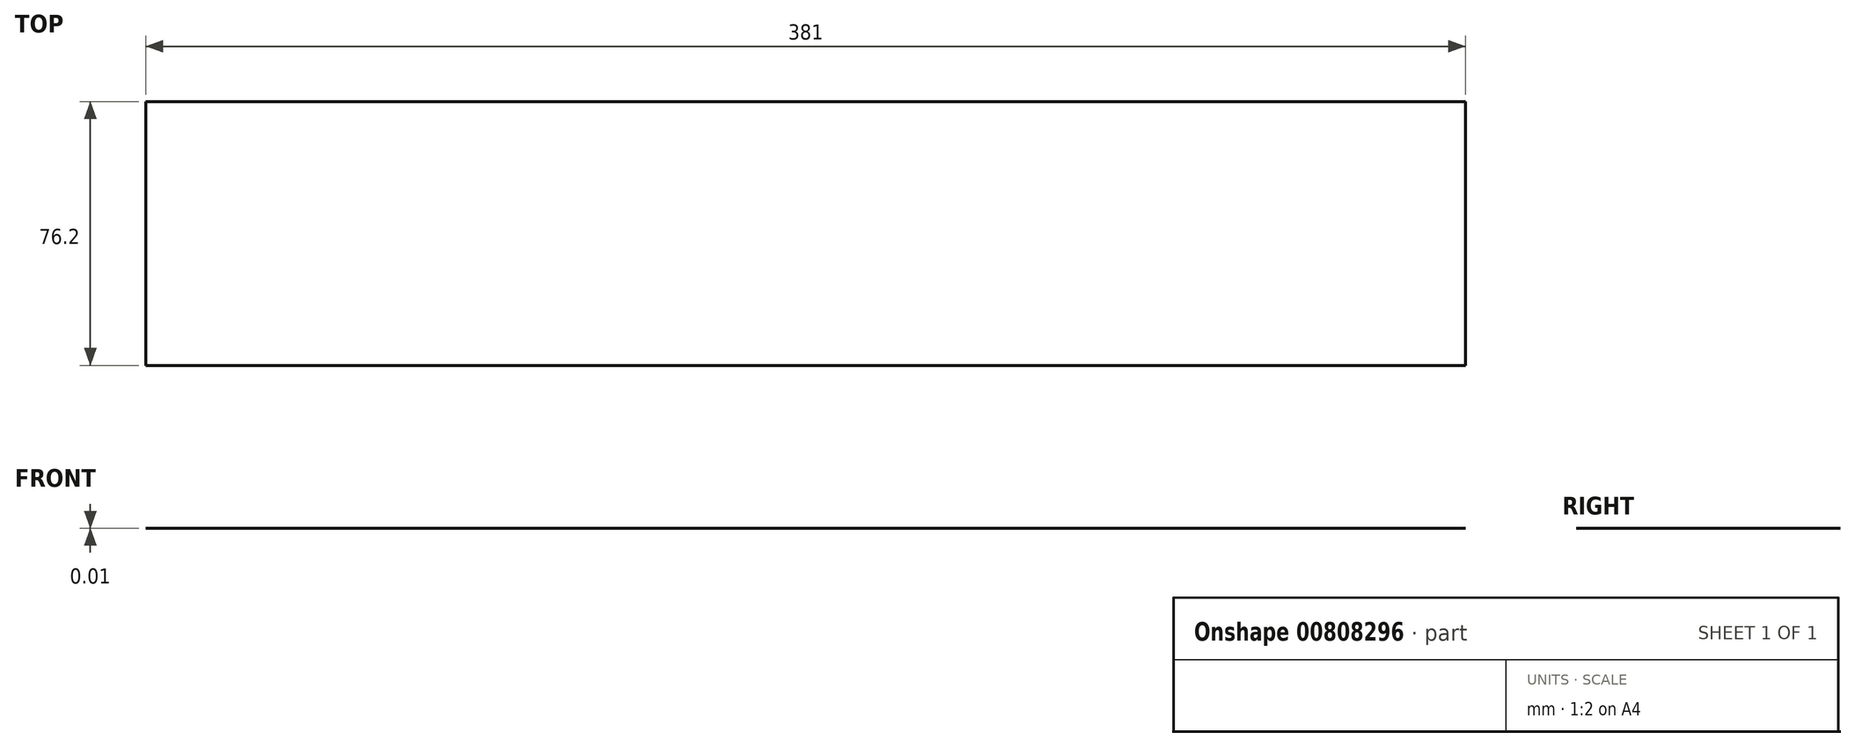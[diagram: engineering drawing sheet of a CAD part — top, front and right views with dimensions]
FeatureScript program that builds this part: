
annotation { "Feature Type Name" : "Feature", "Feature Type Description" : "" }
export const myFeature = defineFeature(function(context is Context, id is Id, definition is map)
    precondition{}
    {
        {
            var Q0;
            Q0=qCreatedBy(makeId("Top.planeOp"),FACE);
            var sketch = newSketch(context, id + "F0", { "sketchPlane" : qUnion([Q0])});
            skLineSegment(sketch, "E0.bottom", {"start": v(190.5, -38.1) * mm, "end": v(-190.5, -38.1) * mm});
            skLineSegment(sketch, "E0.top", {"start": v(190.5, 38.1) * mm, "end": v(-190.5, 38.1) * mm});
            skLineSegment(sketch, "E0.left", {"start": v(190.5, -38.1) * mm, "end": v(190.5, 38.1) * mm});
            skLineSegment(sketch, "E0.right", {"start": v(-190.5, -38.1) * mm, "end": v(-190.5, 38.1) * mm});
            skPoint(sketch, "E0.middle", {"position": v(0, 0) * mm});
            skSolve(sketch);
        }
        {
            var Q0;
            Q0=qSketchRegion(id+"F0",true);
            extrude(context, id + "F1", {"entities" : qUnion([Q0]), "depth" : 3 / 203.2 * mm, "offsetDistance" : 25 * mm});
        }
        {
            var Q0;
            Q0=makeQuery(id+"F1.opExtrude","SWEPT_FACE",FACE,{"disambiguationData":[OSD([sQuery(id+"F0.wireOp",EDGE,"E0.left")])]});
            var sketch = newSketch(context, id + "F2", { "sketchPlane" : qUnion([Q0])});
            skLineSegment(sketch, "E1", {"start": v(-38.1, 0) * mm, "end": v(-28.57, 9.53) * mm});
            skLineSegment(sketch, "E2", {"start": v(-28.57, 9.53) * mm, "end": v(-39.38, 14.38) * mm});
            skLineSegment(sketch, "E3", {"start": v(-39.38, 14.38) * mm, "end": v(-42.22, -2.03) * mm});
            skLineSegment(sketch, "E4", {"start": v(-42.22, -2.03) * mm, "end": v(-38.1, 0) * mm});
            skLineSegment(sketch, "E5", {"start": v(0, 0) * mm, "end": v(0, 9.53) * mm, "construction": true});
            skLineSegment(sketch, "E6.MirrorCS", {"start": v(39.38, 14.38) * mm, "end": v(42.22, -2.03) * mm});
            skLineSegment(sketch, "E7.MirrorCS", {"start": v(42.22, -2.03) * mm, "end": v(38.1, 0) * mm});
            skLineSegment(sketch, "E8.MirrorCS", {"start": v(28.58, 9.52) * mm, "end": v(39.38, 14.38) * mm});
            skLineSegment(sketch, "E9.MirrorCS", {"start": v(38.1, 0) * mm, "end": v(28.58, 9.52) * mm});
            skSolve(sketch);
        }
        {
            var Q0;
            Q0 = qSketchRegion(id + "F2", true);
            extrude(context, id + "F3", {"entities" : qUnion([Q0]), "operationType" : NewBodyOperationType.REMOVE, "endBound" : BoundingType.THROUGH_ALL, "oppositeDirection" : true, "depth" : 25.4 * mm, "offsetDistance" : 25.4 * mm});
        }
    });
